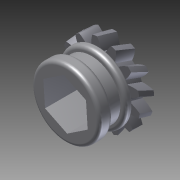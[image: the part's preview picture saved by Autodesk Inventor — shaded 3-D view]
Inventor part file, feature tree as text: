
AUTODESK INVENTOR PART (.ipt)
format: ipt  version: 2012 (Build 160160000, 160)  size: 715,264 bytes
history: native  units: in
note: dims shown in document units (in); Inventor stores cm internally (conversion verified against a paired STEP export)
features: sketch x8, extrude x8, fillet x6, other x3, plane x3
ambient origin geometry x8: Origin, YZ Plane, XZ Plane, XY Plane, X Axis, Y Axis, Z Axis, Center Point
bodies: Solid1 (feature_tree)
feature tree (28):
  other  "LargeGearInput.iam"
  other  "Spur Gear2:1"
  other  "BlankLargeGearMotorInput.ipt:1"
  plane  "Work Plane1"
  sketch  "Sketch4"  dims[d0=0.3937in d5=0.3937in d6=0.0in]
  plane  "Work Plane2"
  extrude  "Extrusion3"  Depth=0.3937in TaperAngle=0.0deg
  extrude  "Extrusion4"  Depth=0.6496in
  extrude  "Extrusion5"  Depth=0.3937in TaperAngle=0.0deg
  extrude  "Extrusion6"  Depth=0.2402in
  extrude  "Extrusion7"  Depth=0.3937in TaperAngle=0.0deg
  extrude  "Extrusion8"  Depth=0.1378in TaperAngle=0.0deg
  plane  "Work Plane3"
  extrude  "Extrusion9"  Depth=0.0787in TaperAngle=0.0deg
  fillet  "Fillet2"  Radius=0.0197in
  fillet  "Fillet3"  Radius=0.0151in
  fillet  "Fillet4"  Radius=0.0394in
  fillet  "Fillet5"  Radius=0.0197in
  extrude  "Extrusion10"  Depth=0.0394in
  fillet  "Fillet6"  Radius=0.0394in
  fillet  "Fillet7"  [1 undecoded]
  sketch  "Sketch5"  dims[d7=0.0118in d8=0.0in d9=0.6496in]
  sketch  "Sketch6"  dims[d10=0.4803in d11=0.3937in d12=0.0in]
  sketch  "Sketch7"  dims[d13=0.3937in d14=0.0in d15=0.2402in]
  sketch  "Sketch8"  dims[d16=0.4803in d17=0.3937in d18=0.0in]
  sketch  "Sketch10"  dims[d19=0.0591in d20=0.1378in d21=0.0in]
  sketch  "Sketch11"  dims[d22=0.1535in d23=0.0787in d24=0.0in d26=0.0197in d27=0.0151in d28=0.0394in d29=0.0197in]
  sketch  "Sketch12"  dims[d30=0.0118in d31=0.0in d32=0.0394in d33=0.0394in]
note: 1 required parameter value undecoded (feature->parameter linkage not recoverable at this tier; creation-order binding heuristic only, values carry confidence <= 0.55)
